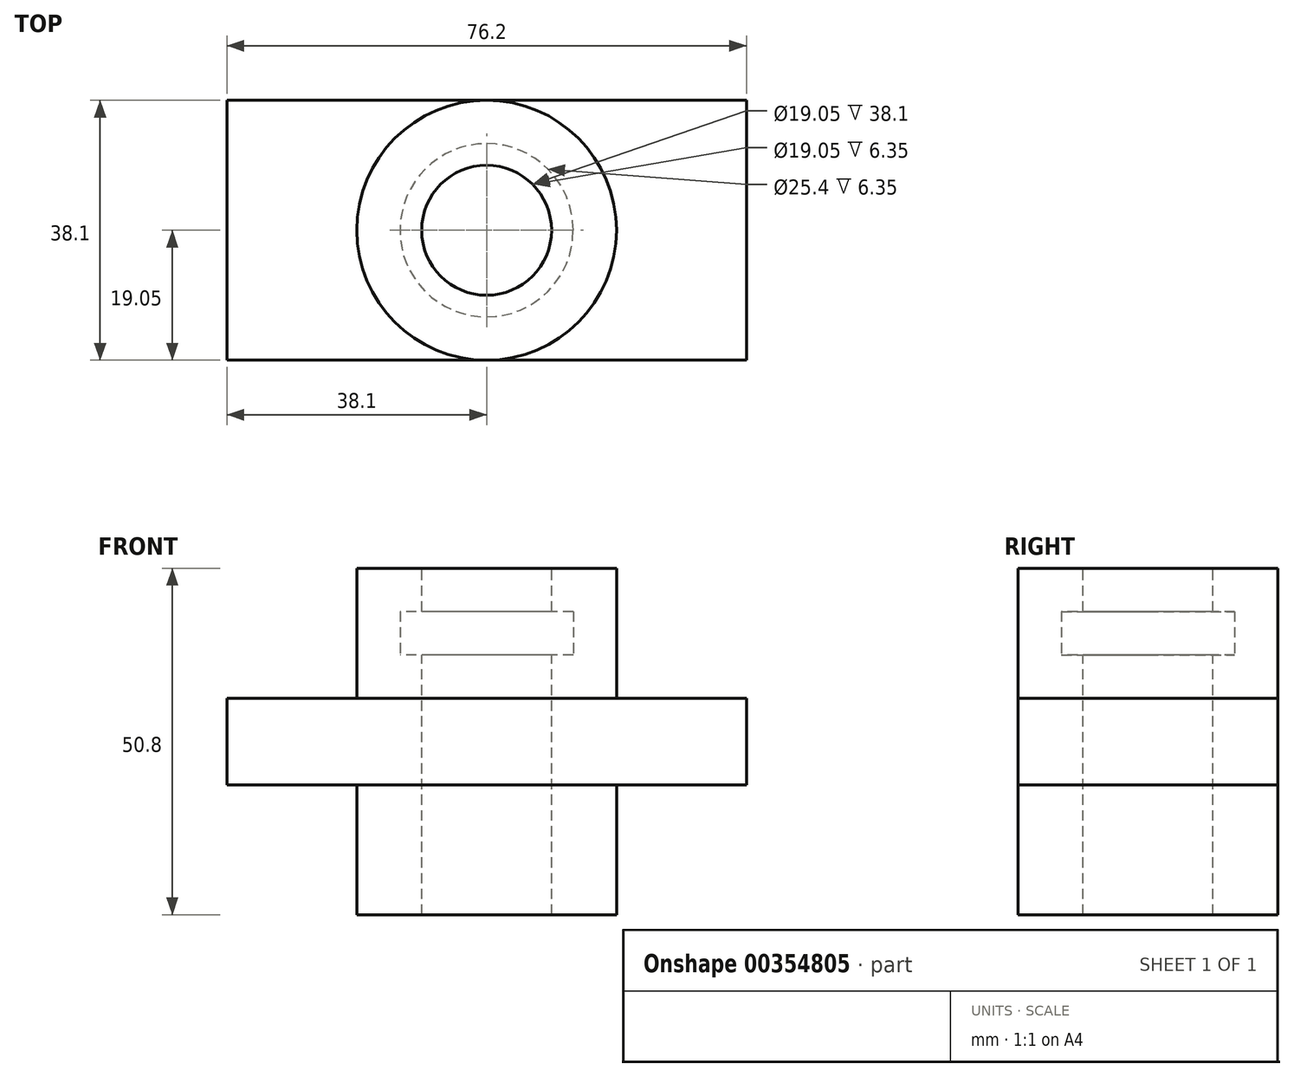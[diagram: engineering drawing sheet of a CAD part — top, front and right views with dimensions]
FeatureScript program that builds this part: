
annotation { "Feature Type Name" : "Feature", "Feature Type Description" : "" }
export const myFeature = defineFeature(function(context is Context, id is Id, definition is map)
    precondition{}
    {
        {
            var Q0;
            Q0=qCreatedBy(makeId("Top.planeOp"),FACE);
            var sketch = newSketch(context, id + "F0", { "sketchPlane" : qUnion([Q0])});
            skLineSegment(sketch, "E0.bottom", {"start": v(-38.1, 19.05) * mm, "end": v(38.1, 19.05) * mm});
            skLineSegment(sketch, "E0.top", {"start": v(-38.1, -19.05) * mm, "end": v(38.1, -19.05) * mm});
            skLineSegment(sketch, "E0.left", {"start": v(-38.1, 19.05) * mm, "end": v(-38.1, -19.05) * mm});
            skLineSegment(sketch, "E0.right", {"start": v(38.1, 19.05) * mm, "end": v(38.1, -19.05) * mm});
            skCircle(sketch, "E1", {"center": v(0, 0) * mm, "radius": 19.05 * mm});
            skSolve(sketch);
        }
        {
            var Q0;
            {var subQ0=sQuery(id+"F0.wireOp",EDGE,"E1");var subQ1=makeQuery(id+"F0.imprint","INTERSECT",VERTEX,{"derivedFrom":[sQuery(id+"F0.wireOp",EDGE,"E0.bottom"),subQ0]});Q0=makeQuery(id+"F0.imprint","IMPRINT",FACE,{"disambiguationData":[TD([[makeQuery(id+"F0.imprint","IMPRINT",EDGE,{"disambiguationData":[TD([[subQ1,-1.0]])],"derivedFrom":subQ0}),1.0]])]});}
            extrude(context, id + "F1", {"entities" : qUnion([Q0]), "endBound" : BoundingType.SYMMETRIC, "depth" : 50.8 * mm});
        }
        {
            var Q0;
            {var subQ0=sQuery(id+"F0.wireOp",EDGE,"E0.left");Q0=makeQuery(id+"F0.imprint","IMPRINT",FACE,{"disambiguationData":[TD([[makeQuery(id+"F0.imprint","IMPRINT",EDGE,{"derivedFrom":subQ0}),1.0]])]});}
            var Q1;
            {var subQ0=sQuery(id+"F0.wireOp",EDGE,"E0.right");Q1=makeQuery(id+"F0.imprint","IMPRINT",FACE,{"disambiguationData":[TD([[makeQuery(id+"F0.imprint","IMPRINT",EDGE,{"derivedFrom":subQ0}),-1.0]])]});}
            extrude(context, id + "F2", {"entities" : qUnion([Q0, Q1]), "operationType" : NewBodyOperationType.ADD, "endBound" : BoundingType.SYMMETRIC, "depth" : 12.7 * mm});
        }
        {
            var Q0;
            Q0=qCreatedBy(makeId("Top.planeOp"),FACE);
            var sketch = newSketch(context, id + "F3", { "sketchPlane" : qUnion([Q0])});
            skCircle(sketch, "E2", {"center": v(0, 0) * mm, "radius": 12.7 * mm});
            skSolve(sketch);
        }
        {
            var Q0;
            Q0 = qSketchRegion(id + "F3", true);
            extrude(context, id + "F4", {"entities" : qUnion([Q0]), "operationType" : NewBodyOperationType.REMOVE, "depth" : 19.05 * mm});
        }
        {
            var Q0;
            Q0=qCreatedBy(makeId("Top.planeOp"),FACE);
            var sketch = newSketch(context, id + "F5", { "sketchPlane" : qUnion([Q0])});
            skCircle(sketch, "E3", {"center": v(0, 0) * mm, "radius": 12.7 * mm});
            skSolve(sketch);
        }
        {
            var Q0;
            Q0=makeQuery(id+"F5.imprint","IMPRINT",FACE,{"disambiguationData":[TD([[makeQuery(id+"F5.imprint","IMPRINT",EDGE,{"derivedFrom":sQuery(id+"F5.wireOp",EDGE,"E3")}),1.0]])]});
            extrude(context, id + "F6", {"entities" : qUnion([Q0]), "operationType" : NewBodyOperationType.ADD, "depth" : 12.7 * mm});
        }
        {
            var Q0;
            Q0=makeQuery(id+"F1.opExtrude","CAP_FACE",FACE,{"disambiguationData":[OSD([sQuery(id+"F0.wireOp",EDGE,"E1")])],"isStart":false});
            var sketch = newSketch(context, id + "F7", { "sketchPlane" : qUnion([Q0])});
            skCircle(sketch, "E4", {"center": v(0, 0) * mm, "radius": 9.53 * mm});
            skSolve(sketch);
        }
        {
            var Q0;
            Q0 = qSketchRegion(id + "F7", true);
            extrude(context, id + "F8", {"entities" : qUnion([Q0]), "operationType" : NewBodyOperationType.REMOVE, "endBound" : BoundingType.THROUGH_ALL, "oppositeDirection" : true, "depth" : 25.4 * mm});
        }
    });
